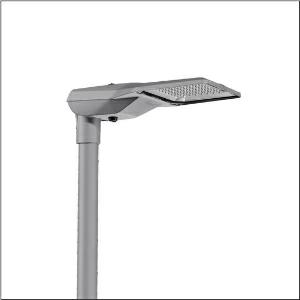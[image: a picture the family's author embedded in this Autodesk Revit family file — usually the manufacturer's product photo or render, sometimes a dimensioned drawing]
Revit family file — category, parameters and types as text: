
# Revit family: streetlight_sl_21_iq_midi___pc-r_5xe3g31y08mb_65a2
name_source: partatom
category: Lighting Fixtures
units: mm (PartAtom-declared; Revit-internal decimal feet)

## family parameters
Cut with Voids When Loaded = No
Host = Face
Light Source = No
Part Type = Normal
Room Calculation Point = No
Round Connector Dimension = Use Diameter
Shared = No

## types (1)
- --- (1 x LED, 17070 lm, 129.3 W, 3000K)
    Apparent Load = 129 VA
    CIE Flux Codes = 38 78 98 100 100
    Color Rendering = 70
    Color Temperature = 3000K
    Default Elevation = 1800 mm
    Description = Streetlight SL 21 iQ midi, mast luminaire, primary light control with lens, of PMMA, primary optical cover: cover, of toughened safety glass, transparent, light distribution: PC-R, light emission: direct distribution, primary light characteristic: asymmetric, right, installation type: post-top, side-entry, LED, High Power LED, rated luminous flux: 17.070lm, luminous efficacy: 132lm/W, light colour: 730, colour temperature: 3000K, control: pre-setting: logarithmic dimming characteristic, Street-Remote, Auto-Match, Temp-Guard, Lumen-Switch, Night-Set, Smart-Wire, Light-Fading, Desk-Remote (wireless, voltage-free reading and setting of iQ features in the workshop via application-optimized NFC function/RFID function), optimised constant luminous flux control (CLO 2.0), mains connection: 230..240V, AC, 50/60Hz, start of lifetime: 129W, end of service life: 142W, reduction: 56W, luminaire housing, of diecast aluminium, powder-coated, Siteco® metallic grey (DB 702S), corrosivity category C5 mid according to DIN EN ISO 12944, please order mast flange separately, inclination adjustable: 0°, 5°, 10°, 15°, sealing non-destructively replaceable, multi-level sealing system, length: 644mm, width: 335mm, height: 110mm, mast flange for spigot size: 42mm (side-entry): 5XC10008XM4, 60/48mm (side-entry/post-top): 5XC10108XM2, 76/60mm (side-entry/post-top): 5XC10108XM1, Smart Interface below and above, protection rating (complete): IP66, insulation class (complete): insulation class II (safety insulation), certification: CE, ENEC, ENEC+, VDE, impact resistance: IK09, permissible operating ambient temperature for outdoor applications: -40..+50°C, standard-compliant lighting for roads and squares, packaging unit: 1 piece

Light Distribution: PC-R
    Height = 111 mm
    Lamp = 1 x LED
    Lamp Light Flux = 17070 lm
    Lamp Power = 129.3 W
    Lamp count = 1
    Length = 644 mm
    Luminous efficacy = 132 lm/W
    Manufacturer = Siteco
    ModVariant = No
    Model = 5XE3G31Y08MB
    Number of Poles = 1
    OnlyDefault = Yes
    Power Factor = 1
    Product Name = Streetlight SL 21 iQ midi | PC-R
    Product group = mast luminaire | pylon top
    ProductGroupID = 6100
    Protection Class = Protection class II
    Protection Degree = IP 66
    RLX_Detail_Level = 1
    RLX_Emergency_Light_Flux = 0 lm
    RLX_Emergency_Type = 0
    RLX_Emergency_Type_DB = No
    RlxData = <blob elided: 93413 chars, md5=e2459c92>
    Socket = socket
    Standby Power = 0 W
    System Light Flux = 17070 lm
    System Power = 129 W
    Type Comments = factory setting: luminous flux: 100 % | dim-lin: 254 | 672 mA
    Type Image = l_1004304.jpg
    URL = http://relux.com
    VarID = @adj_032383
    Voltage = 0 V
    Weight = 0.00 kg
    Width = 336 mm

## geometry (parser evidence)
native form markers: Blend x4, Sweep x10
no freeform markers — native parametric forms only
